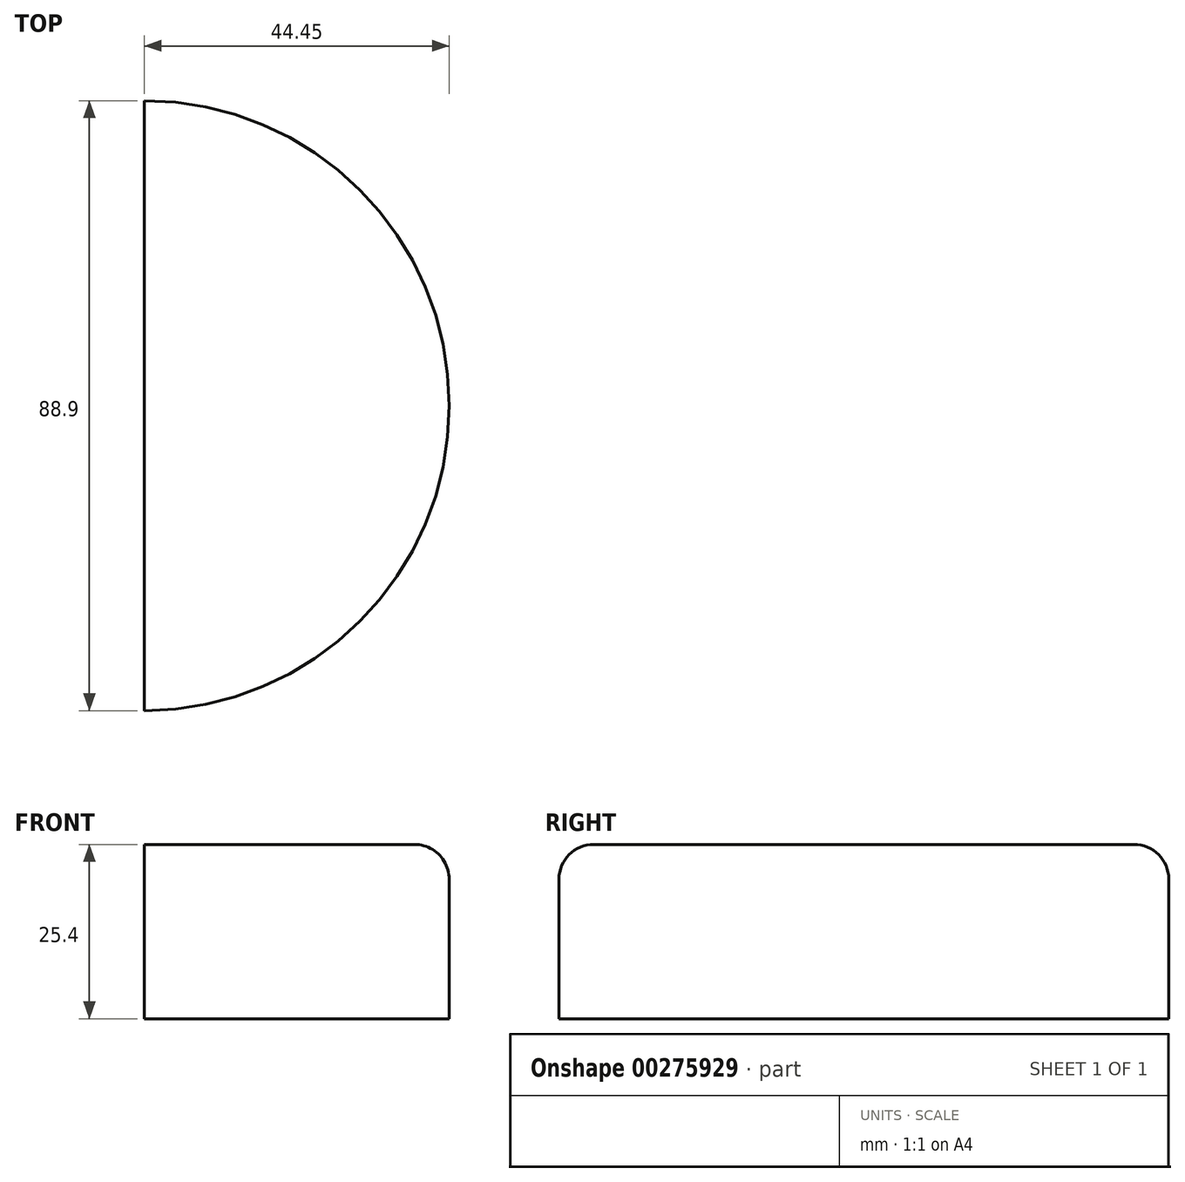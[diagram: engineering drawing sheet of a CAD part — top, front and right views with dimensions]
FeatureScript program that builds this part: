
annotation { "Feature Type Name" : "Feature", "Feature Type Description" : "" }
export const myFeature = defineFeature(function(context is Context, id is Id, definition is map)
    precondition{}
    {
        {
            var Q0;
            Q0=qCreatedBy(makeId("Top.planeOp"),FACE);
            var sketch = newSketch(context, id + "F0", { "sketchPlane" : qUnion([Q0])});
            skArc(sketch, "E0", {"start": v(0, 44.45) * mm, "mid": v(44.45, 0) * mm, "end": v(0, -44.45) * mm});
            skLineSegment(sketch, "E1", {"start": v(0, 44.45) * mm, "end": v(0, -44.45) * mm});
            skSolve(sketch);
        }
        {
            var Q0;
            Q0=qSketchRegion(id+"F0",true);
            extrude(context, id + "F1", {"entities" : qUnion([Q0]), "endBound" : BoundingType.SYMMETRIC, "depth" : 25.4 * mm});
        }
        {
            var Q0;
            Q0=makeQuery(id+"F1.opExtrude","CAP_EDGE",EDGE,{"disambiguationData":[OSD([sQuery(id+"F0.wireOp",EDGE,"E0")])],"isStart":false});
            fillet(context, id + "F2", {"entities" : qUnion([Q0]), "radius" : 5.08 * mm, "tangentPropagation" : true, "allowEdgeOverflow" : false});
        }
    });
